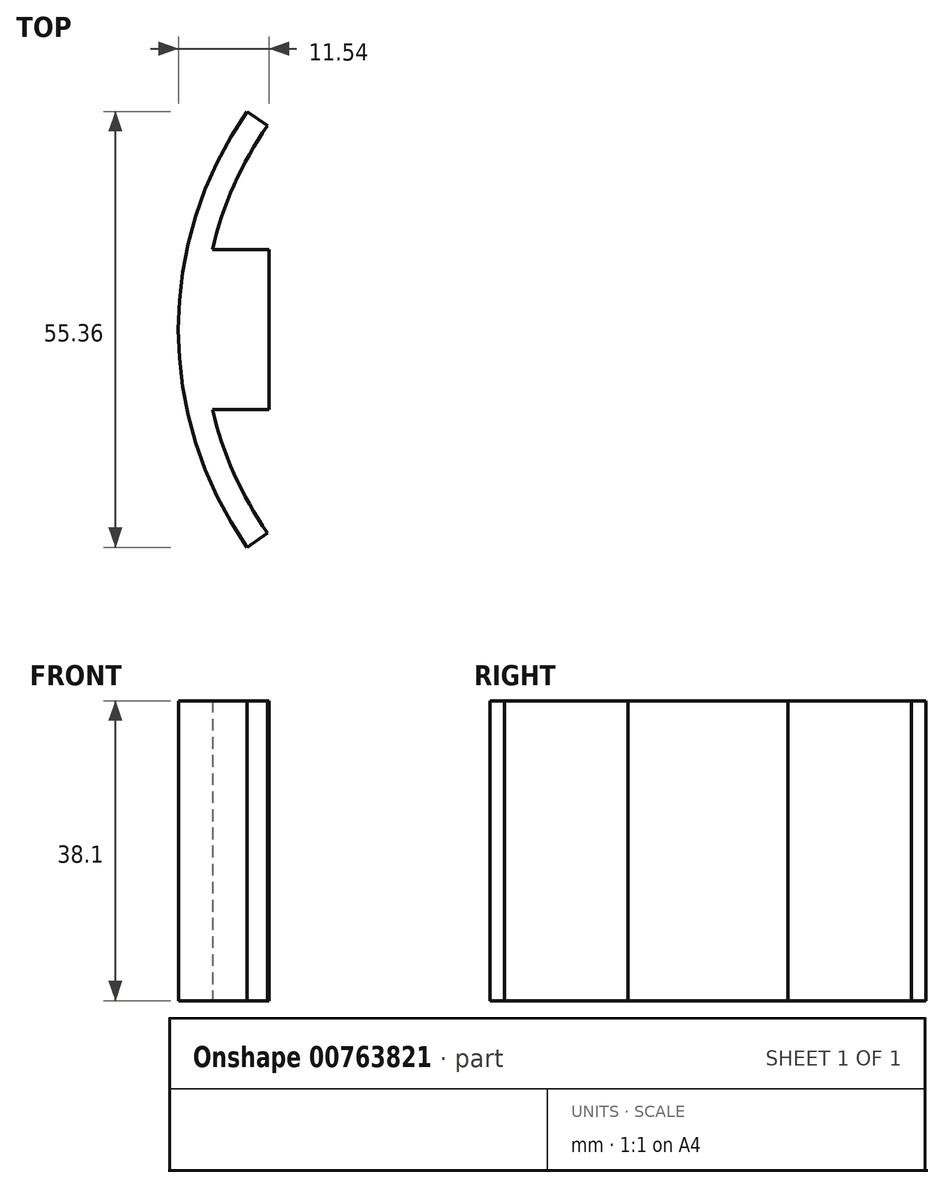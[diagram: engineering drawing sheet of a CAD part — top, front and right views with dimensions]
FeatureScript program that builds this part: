
annotation { "Feature Type Name" : "Feature", "Feature Type Description" : "" }
export const myFeature = defineFeature(function(context is Context, id is Id, definition is map)
    precondition{}
    {
        {
            var Q0;
            Q0=qCreatedBy(makeId("Top.planeOp"),FACE);
            var sketch = newSketch(context, id + "F0", { "sketchPlane" : qUnion([Q0])});
            skArc(sketch, "E0", {"start": v(-43.93, -10.16) * mm, "mid": v(-41.18, -18.35) * mm, "end": v(-36.93, -25.86) * mm});
            skArc(sketch, "E1", {"start": v(-39.53, 27.68) * mm, "mid": v(-48.26, 0) * mm, "end": v(-39.53, -27.68) * mm});
            skLineSegment(sketch, "E2", {"start": v(-43.93, 10.16) * mm, "end": v(-36.72, 10.16) * mm});
            skLineSegment(sketch, "E3.MirrorCS", {"start": v(-43.93, -10.16) * mm, "end": v(-36.72, -10.16) * mm});
            skLineSegment(sketch, "E4", {"start": v(-36.72, 10.16) * mm, "end": v(-36.72, -10.16) * mm});
            skLineSegment(sketch, "E5", {"start": v(-36.93, 25.86) * mm, "end": v(-39.53, 27.68) * mm});
            skLineSegment(sketch, "E6", {"start": v(-36.93, -25.86) * mm, "end": v(-39.53, -27.68) * mm});
            skArc(sketch, "E7.trimOffspring", {"start": v(-36.93, 25.86) * mm, "mid": v(-41.18, 18.35) * mm, "end": v(-43.93, 10.16) * mm});
            skSolve(sketch);
        }
        {
            var Q0;
            Q0 = qSketchRegion(id + "F0", true);
            extrude(context, id + "F1", {"entities" : qUnion([Q0]), "depth" : 38.1 * mm, "offsetDistance" : 25.4 * mm});
        }
    });
